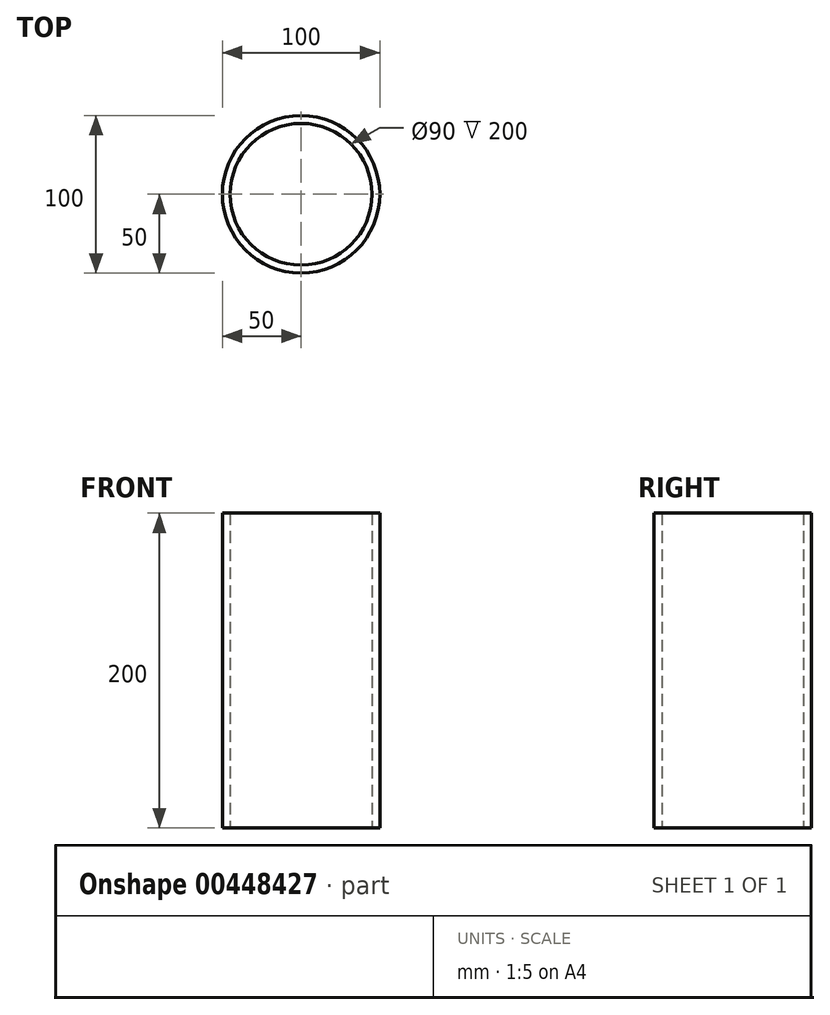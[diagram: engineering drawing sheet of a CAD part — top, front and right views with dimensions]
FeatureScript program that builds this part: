
annotation { "Feature Type Name" : "Feature", "Feature Type Description" : "" }
export const myFeature = defineFeature(function(context is Context, id is Id, definition is map)
    precondition{}
    {
        {
            var Q0;
            Q0=qCreatedBy(makeId("Top.planeOp"),FACE);
            var sketch = newSketch(context, id + "F0", { "sketchPlane" : qUnion([Q0])});
            skCircle(sketch, "E0", {"center": v(0, 0) * mm, "radius": 50 * mm});
            skCircle(sketch, "E1", {"center": v(0, 0) * mm, "radius": 45 * mm});
            skSolve(sketch);
        }
        {
            var Q0;
            Q0 = qSketchRegion(id + "F0", true);
            extrude(context, id + "F1", {"entities" : qUnion([Q0]), "depth" : 200 * mm});
        }
    });
